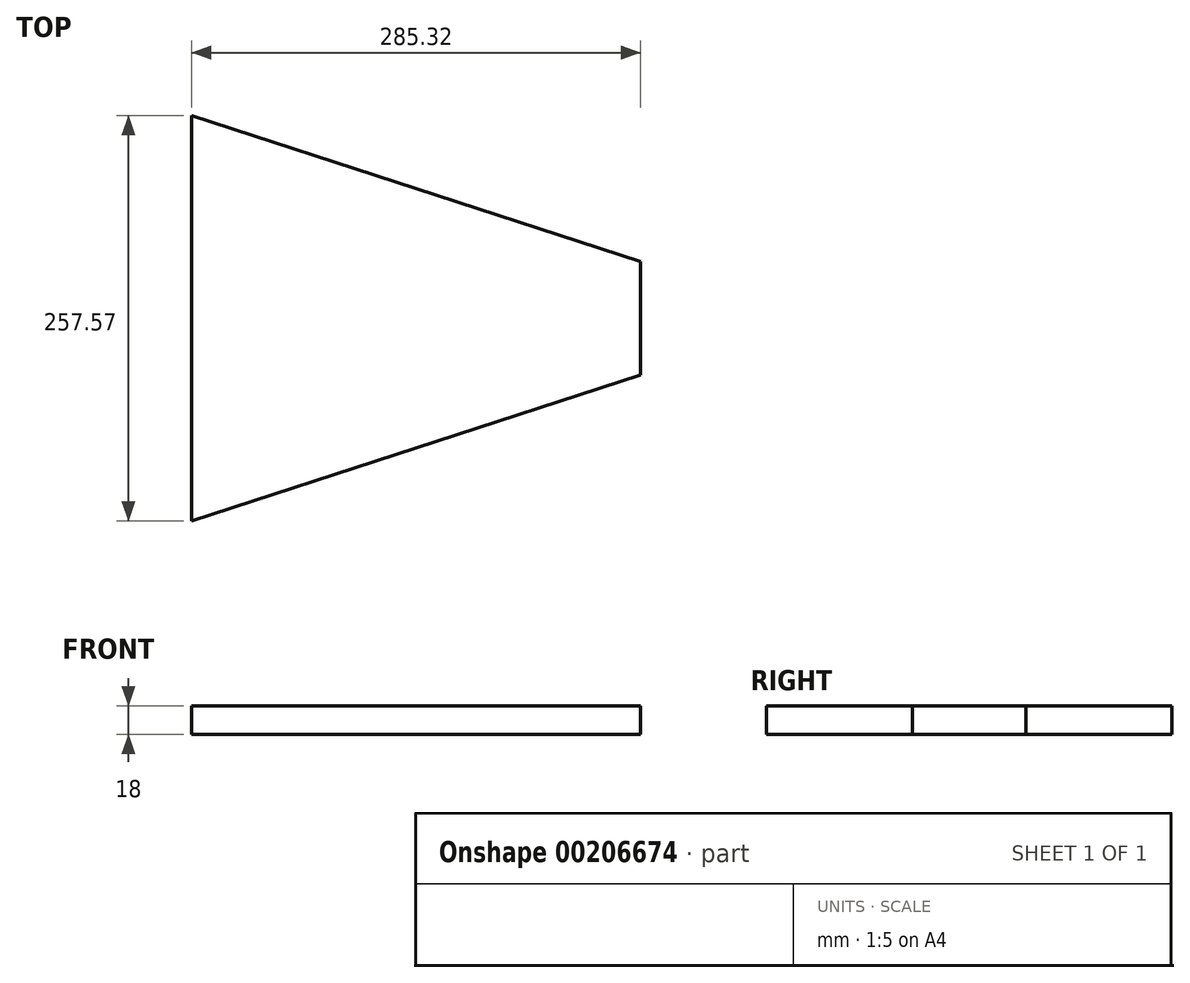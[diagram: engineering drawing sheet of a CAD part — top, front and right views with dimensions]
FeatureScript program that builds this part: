
annotation { "Feature Type Name" : "Feature", "Feature Type Description" : "" }
export const myFeature = defineFeature(function(context is Context, id is Id, definition is map)
    precondition{}
    {
        {
            var Q0;
            Q0=qCreatedBy(makeId("Top.planeOp"),FACE);
            var sketch = newSketch(context, id + "F0", { "sketchPlane" : qUnion([Q0])});
            skLineSegment(sketch, "E0.bottom", {"start": v(-600, 150) * mm, "end": v(600, 150) * mm, "construction": true});
            skLineSegment(sketch, "E0.top", {"start": v(-600, -150) * mm, "end": v(600, -150) * mm, "construction": true});
            skLineSegment(sketch, "E0.left", {"start": v(-600, 150) * mm, "end": v(-600, -150) * mm, "construction": true});
            skLineSegment(sketch, "E0.right", {"start": v(600, 150) * mm, "end": v(600, -150) * mm, "construction": true});
            skPoint(sketch, "E0.middle", {"position": v(0, 0) * mm});
            skLineSegment(sketch, "E1", {"start": v(-600, 150) * mm, "end": v(0, 150) * mm});
            skLineSegment(sketch, "E2", {"start": v(0, 150) * mm, "end": v(0, -150) * mm});
            skLineSegment(sketch, "E3", {"start": v(0, -150) * mm, "end": v(-130.9, -150) * mm});
            skLineSegment(sketch, "E4", {"start": v(-130.9, -150) * mm, "end": v(-100, -54.9) * mm});
            skLineSegment(sketch, "E5", {"start": v(-100, -54.9) * mm, "end": v(-600, 107.57) * mm});
            skLineSegment(sketch, "E6", {"start": v(-600, 107.57) * mm, "end": v(-600, 150) * mm});
            skLineSegment(sketch, "E7", {"start": v(-600, -150) * mm, "end": v(-314.68, -57.3) * mm});
            skLineSegment(sketch, "E8", {"start": v(-314.68, -57.3) * mm, "end": v(-314.68, 14.86) * mm});
            skLineSegment(sketch, "E9", {"start": v(-314.68, 14.86) * mm, "end": v(-600, 107.57) * mm});
            skLineSegment(sketch, "E10", {"start": v(-600, 107.57) * mm, "end": v(-600, -150) * mm});
            skPoint(sketch, "E11.endSnap0", {"position": v(-314.68, -21.22) * mm});
            skPoint(sketch, "E11.endSnap1", {"position": v(-600, -21.22) * mm});
            skLineSegment(sketch, "E12", {"start": v(-314.68, -21.22) * mm, "end": v(-600, -21.22) * mm, "construction": true});
            skLineSegment(sketch, "E13", {"start": v(600, 107.57) * mm, "end": v(100, -54.9) * mm});
            skLineSegment(sketch, "E14", {"start": v(100, -54.9) * mm, "end": v(130.9, -150) * mm});
            skLineSegment(sketch, "E15", {"start": v(130.9, -150) * mm, "end": v(0, -150) * mm});
            skLineSegment(sketch, "E16", {"start": v(600, 150) * mm, "end": v(600, 107.57) * mm});
            skLineSegment(sketch, "E17", {"start": v(0, -150) * mm, "end": v(0, -200) * mm});
            skLineSegment(sketch, "E18", {"start": v(0, -200) * mm, "end": v(-210.24, -200) * mm});
            skLineSegment(sketch, "E19", {"start": v(-210.24, -200) * mm, "end": v(-187.97, -131.46) * mm});
            skLineSegment(sketch, "E20", {"start": v(-187.97, -131.46) * mm, "end": v(-130.9, -150) * mm});
            skLineSegment(sketch, "E21", {"start": v(-130.9, -150) * mm, "end": v(0, -150) * mm});
            skSolve(sketch);
        }
        {
            var Q0;
            Q0=makeQuery(id+"F0.imprint","IMPRINT",FACE,{"disambiguationData":[TD([[makeQuery(id+"F0.imprint","IMPRINT",EDGE,{"derivedFrom":sQuery(id+"F0.wireOp",EDGE,"E7")}),1.0]])]});
            extrude(context, id + "F1", {"entities" : qUnion([Q0]), "depth" : 18 * mm});
        }
    });
